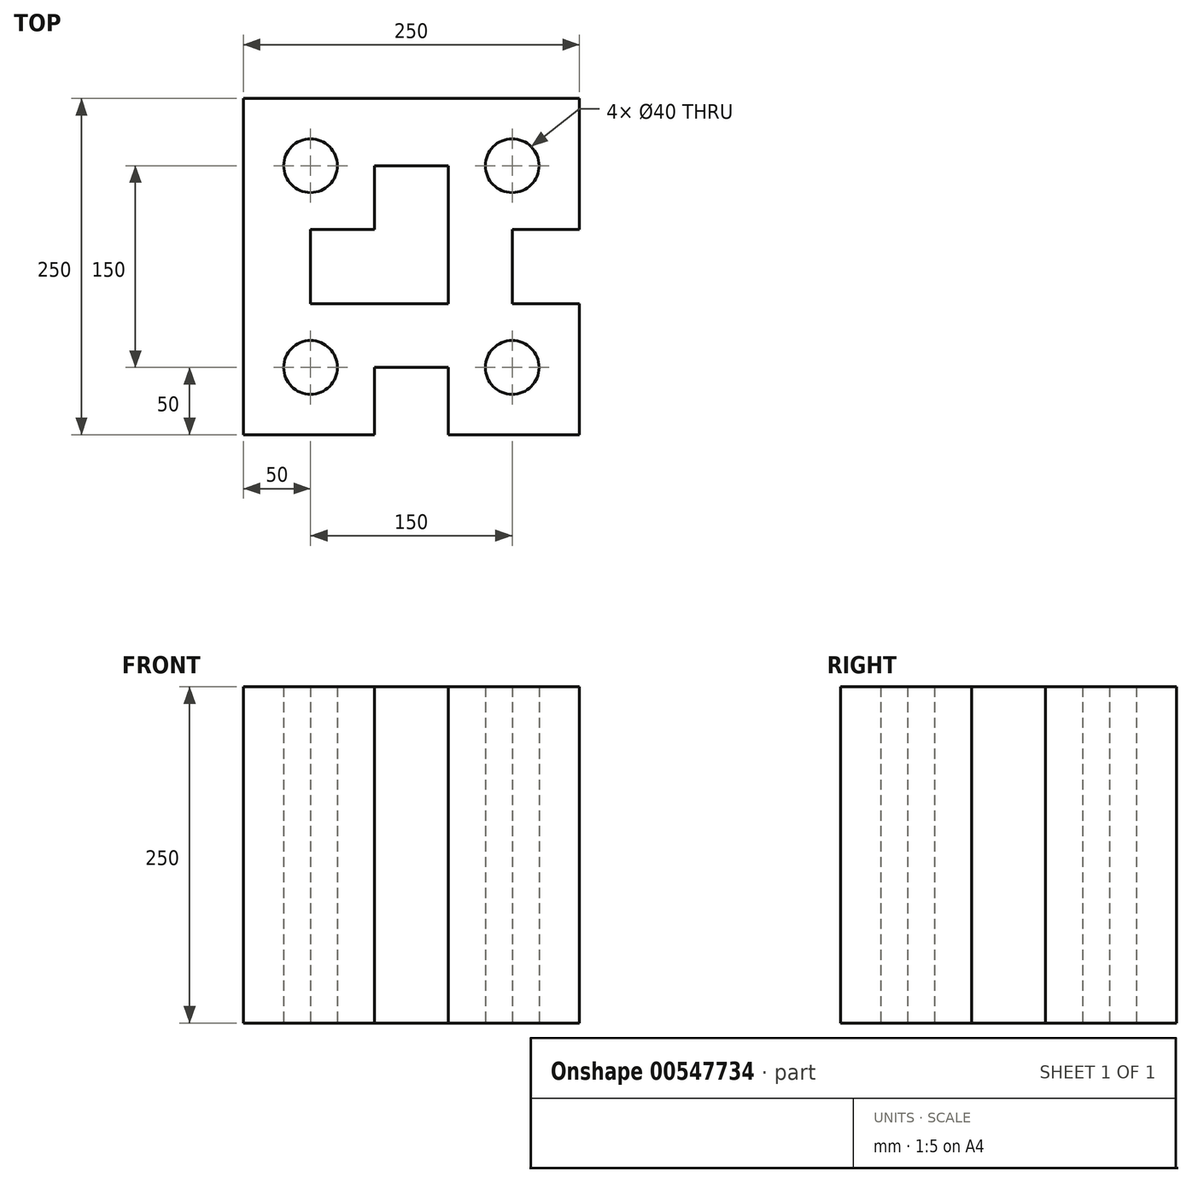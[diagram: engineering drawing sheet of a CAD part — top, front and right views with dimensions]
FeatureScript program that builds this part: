
annotation { "Feature Type Name" : "Feature", "Feature Type Description" : "" }
export const myFeature = defineFeature(function(context is Context, id is Id, definition is map)
    precondition{}
    {
        {
            var Q0;
            Q0=qCreatedBy(makeId("Top.planeOp"),FACE);
            var sketch = newSketch(context, id + "F0", { "sketchPlane" : qUnion([Q0])});
            skLineSegment(sketch, "E0.bottom", {"start": v(125, -125) * mm, "end": v(27.5, -125) * mm});
            skLineSegment(sketch, "E0.top", {"start": v(125, 125) * mm, "end": v(-125, 125) * mm});
            skLineSegment(sketch, "E0.left", {"start": v(125, -125) * mm, "end": v(125, -27.5) * mm});
            skLineSegment(sketch, "E0.right", {"start": v(-125, -125) * mm, "end": v(-125, 125) * mm});
            skLineSegment(sketch, "E1", {"start": v(0, 0) * mm, "end": v(0, -125) * mm, "construction": true});
            skLineSegment(sketch, "E2", {"start": v(0, 0) * mm, "end": v(125, 0) * mm, "construction": true});
            skLineSegment(sketch, "E3.top", {"start": v(27.5, -75) * mm, "end": v(-27.5, -75) * mm});
            skLineSegment(sketch, "E3.left", {"start": v(27.5, -125) * mm, "end": v(27.5, -75) * mm});
            skLineSegment(sketch, "E3.right", {"start": v(-27.5, -125) * mm, "end": v(-27.5, -75) * mm});
            skPoint(sketch, "E3.middle", {"position": v(0, -100) * mm});
            skLineSegment(sketch, "E4.trimOffspring", {"start": v(-27.5, -125) * mm, "end": v(-125, -125) * mm});
            skLineSegment(sketch, "E5.bottom", {"start": v(125, 27.5) * mm, "end": v(75, 27.5) * mm});
            skLineSegment(sketch, "E5.top", {"start": v(125, -27.5) * mm, "end": v(75, -27.5) * mm});
            skLineSegment(sketch, "E5.right", {"start": v(75, 27.5) * mm, "end": v(75, -27.5) * mm});
            skPoint(sketch, "E5.middle", {"position": v(100, 0) * mm});
            skLineSegment(sketch, "E6.trimOffspring", {"start": v(125, 27.5) * mm, "end": v(125, 125) * mm});
            skCircle(sketch, "E7", {"center": v(-75, 75) * mm, "radius": 20 * mm});
            skCircle(sketch, "E8", {"center": v(75, 75) * mm, "radius": 20 * mm});
            skCircle(sketch, "E9", {"center": v(75, -75) * mm, "radius": 20 * mm});
            skCircle(sketch, "E10", {"center": v(-75, -75) * mm, "radius": 20 * mm});
            skLineSegment(sketch, "E11", {"start": v(27.5, -27.5) * mm, "end": v(-75, -27.5) * mm});
            skLineSegment(sketch, "E12", {"start": v(-75, -27.5) * mm, "end": v(-75, 27.5) * mm});
            skLineSegment(sketch, "E13", {"start": v(-75, 27.5) * mm, "end": v(-27.5, 27.5) * mm});
            skLineSegment(sketch, "E14", {"start": v(-27.5, 27.5) * mm, "end": v(-27.5, 75) * mm});
            skLineSegment(sketch, "E15", {"start": v(-27.5, 75) * mm, "end": v(27.5, 75) * mm});
            skLineSegment(sketch, "E16", {"start": v(27.5, 75) * mm, "end": v(27.5, -27.5) * mm});
            skSolve(sketch);
        }
        {
            var Q0;
            Q0=makeQuery(id+"F0.imprint","IMPRINT",FACE,{"disambiguationData":[TD([[makeQuery(id+"F0.imprint","IMPRINT",EDGE,{"derivedFrom":sQuery(id+"F0.wireOp",EDGE,"E0.bottom")}),-1.0]])]});
            extrude(context, id + "F1", {"entities" : qUnion([Q0]), "endBound" : BoundingType.SYMMETRIC, "depth" : 250 * mm, "offsetDistance" : 25 * mm});
        }
    });
